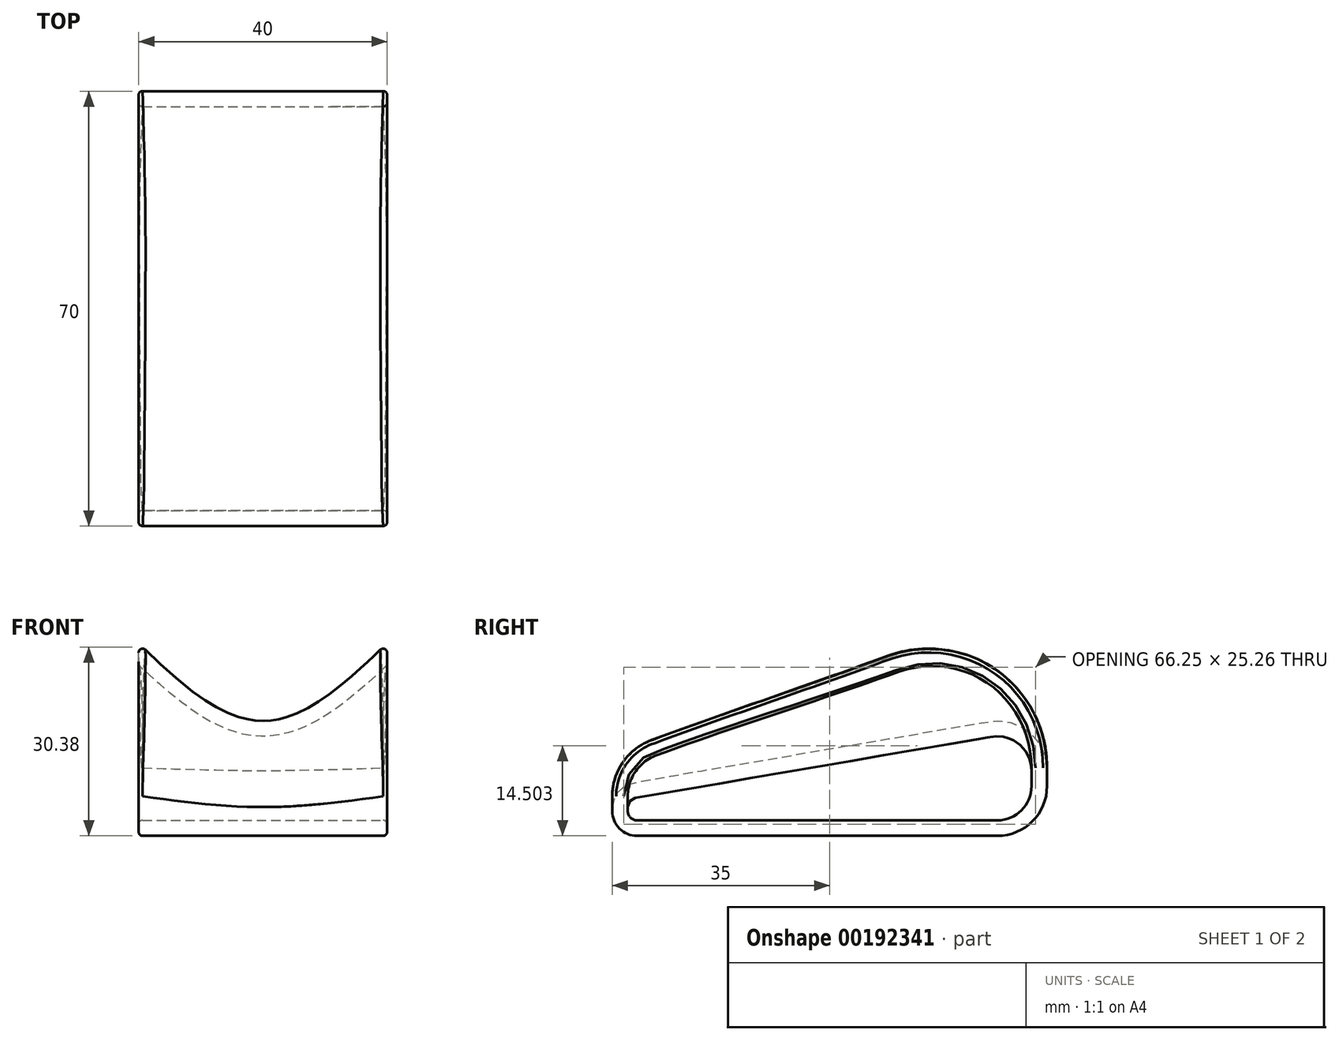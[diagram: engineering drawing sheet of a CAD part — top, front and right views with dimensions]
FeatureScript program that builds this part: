
annotation { "Feature Type Name" : "Feature", "Feature Type Description" : "" }
export const myFeature = defineFeature(function(context is Context, id is Id, definition is map)
    precondition{}
    {
        {
            assignVariable(context, id + "F0", {"name" : "Width", "anyValue" : 40});
        }
        {
            assignVariable(context, id + "F1", {"name" : "Thickness", "anyValue" : 2.5});
        }
        {
            var Q0;
            Q0=qCreatedBy(makeId("Right.planeOp"),FACE);
            var sketch = newSketch(context, id + "F2", { "sketchPlane" : qUnion([Q0])});
            skLineSegment(sketch, "E0", {"start": v(0, 0) * mm, "end": v(27, 0) * mm, "construction": true});
            skLineSegment(sketch, "E1", {"start": v(0, 0) * mm, "end": v(-31, 0) * mm, "construction": true});
            skLineSegment(sketch, "E2", {"start": v(-35, 4) * mm, "end": v(-35, 6.44) * mm, "construction": true});
            skLineSegment(sketch, "E3", {"start": v(35, 8) * mm, "end": v(35, 10.98) * mm, "construction": true});
            skLineSegment(sketch, "E4", {"start": v(7.88, 29.67) * mm, "end": v(-28.56, 15.79) * mm, "construction": true});
            skPoint(sketch, "E5.visualSharp", {"position": v(35, 40) * mm});
            skArc(sketch, "E5.filletArc", {"start": v(35, 10.98) * mm, "mid": v(26.35, 27.45) * mm, "end": v(7.88, 29.67) * mm, "construction": true});
            skPoint(sketch, "E6.visualSharp", {"position": v(-35, 13.33) * mm});
            skArc(sketch, "E6.filletArc", {"start": v(-28.56, 15.79) * mm, "mid": v(-33.23, 12.12) * mm, "end": v(-35, 6.44) * mm, "construction": true});
            skPoint(sketch, "E7.visualSharp", {"position": v(-35, 0) * mm});
            skArc(sketch, "E7.filletArc", {"start": v(-35, 4) * mm, "mid": v(-33.83, 1.17) * mm, "end": v(-31, 0) * mm, "construction": true});
            skPoint(sketch, "E8.visualSharp", {"position": v(35, 0) * mm});
            skArc(sketch, "E8.filletArc", {"start": v(27, 0) * mm, "mid": v(32.66, 2.34) * mm, "end": v(35, 8) * mm, "construction": true});
            skSolve(sketch);
        }
        {
            var Q0;
            Q0=qCreatedBy(makeId("Right.planeOp"),FACE);
            var sketch = newSketch(context, id + "F3", { "sketchPlane" : qUnion([Q0])});
            skLineSegment(sketch, "E9", {"start": v(0, 0) * mm, "end": v(27, 0) * mm, "construction": true});
            skLineSegment(sketch, "E10", {"start": v(0, 0) * mm, "end": v(-31, 0) * mm, "construction": true});
            skLineSegment(sketch, "E11", {"start": v(-35, 4) * mm, "end": v(-35, 4.63) * mm, "construction": true});
            skLineSegment(sketch, "E12", {"start": v(35, 8) * mm, "end": v(35, 10.51) * mm, "construction": true});
            skLineSegment(sketch, "E13", {"start": v(25.65, 18.4) * mm, "end": v(-31.68, 8.57) * mm, "construction": true});
            skPoint(sketch, "E14.visualSharp", {"position": v(35, 20) * mm});
            skArc(sketch, "E14.filletArc", {"start": v(35, 10.51) * mm, "mid": v(32.16, 16.63) * mm, "end": v(25.65, 18.4) * mm, "construction": true});
            skPoint(sketch, "E15.visualSharp", {"position": v(-35, 8) * mm});
            skArc(sketch, "E15.filletArc", {"start": v(-31.68, 8.57) * mm, "mid": v(-34.06, 7.2) * mm, "end": v(-35, 4.63) * mm, "construction": true});
            skPoint(sketch, "E16.visualSharp", {"position": v(-35, 0) * mm});
            skArc(sketch, "E16.filletArc", {"start": v(-35, 4) * mm, "mid": v(-33.83, 1.17) * mm, "end": v(-31, 0) * mm, "construction": true});
            skPoint(sketch, "E17.visualSharp", {"position": v(35, 0) * mm});
            skArc(sketch, "E17.filletArc", {"start": v(27, 0) * mm, "mid": v(32.66, 2.34) * mm, "end": v(35, 8) * mm, "construction": true});
            skSolve(sketch);
        }
        {
            var Q0;
            Q0=qCreatedBy(makeId("Right.planeOp"),FACE);
            cPlane(context, id + "F4", {"entities" : qUnion([Q0]), "cplaneType" : CPlaneType.OFFSET, "offset" : (getVariable(context, 'Width') * 2) * mm, "width" : 150 * mm, "height" : 150 * mm});
        }
        {
            var Q0;
            Q0=qCreatedBy(id+"F4.planeOp",FACE);
            cPlane(context, id + "F5", {"entities" : qUnion([Q0]), "cplaneType" : CPlaneType.OFFSET, "offset" : (getVariable(context, 'Width') / 2) * mm, "width" : 150 * mm, "height" : 150 * mm});
        }
        {
            var Q0;
            Q0=qCreatedBy(id+"F4.planeOp",FACE);
            cPlane(context, id + "F6", {"entities" : qUnion([Q0]), "cplaneType" : CPlaneType.OFFSET, "offset" : (getVariable(context, 'Width') / 2) * mm, "oppositeDirection" : true, "width" : 150 * mm, "height" : 150 * mm});
        }
        {
            var Q0;
            Q0=qCreatedBy(id+"F6.planeOp",FACE);
            var sketch = newSketch(context, id + "F7", { "sketchPlane" : qUnion([Q0])});
            skLineSegment(sketch, "E18.0", {"start": v(0, 0) * mm, "end": v(27, 0) * mm});
            skLineSegment(sketch, "E18.1", {"start": v(0, 0) * mm, "end": v(-31, 0) * mm});
            skLineSegment(sketch, "E18.2", {"start": v(-35, 4) * mm, "end": v(-35, 6.44) * mm});
            skLineSegment(sketch, "E18.3", {"start": v(35, 8) * mm, "end": v(35, 10.98) * mm});
            skLineSegment(sketch, "E18.4", {"start": v(7.88, 29.67) * mm, "end": v(-28.56, 15.79) * mm});
            skPoint(sketch, "E18.5", {"position": v(35, 40) * mm});
            skArc(sketch, "E18.6", {"start": v(35, 10.98) * mm, "mid": v(26.35, 27.45) * mm, "end": v(7.88, 29.67) * mm});
            skPoint(sketch, "E18.7", {"position": v(-35, 13.33) * mm});
            skArc(sketch, "E18.8", {"start": v(-28.56, 15.79) * mm, "mid": v(-33.23, 12.12) * mm, "end": v(-35, 6.44) * mm});
            skPoint(sketch, "E18.9", {"position": v(-35, 0) * mm});
            skArc(sketch, "E18.10", {"start": v(-35, 4) * mm, "mid": v(-33.83, 1.17) * mm, "end": v(-31, 0) * mm});
            skPoint(sketch, "E18.11", {"position": v(35, 0) * mm});
            skArc(sketch, "E18.12", {"start": v(27, 0) * mm, "mid": v(32.66, 2.34) * mm, "end": v(35, 8) * mm});
            skSolve(sketch);
        }
        {
            var Q0;
            Q0=qCreatedBy(id+"F4.planeOp",FACE);
            var sketch = newSketch(context, id + "F8", { "sketchPlane" : qUnion([Q0])});
            skLineSegment(sketch, "E19.0", {"start": v(0, 0) * mm, "end": v(27, 0) * mm});
            skLineSegment(sketch, "E19.1", {"start": v(0, 0) * mm, "end": v(-31, 0) * mm});
            skLineSegment(sketch, "E19.2", {"start": v(-35, 4) * mm, "end": v(-35, 4.63) * mm});
            skLineSegment(sketch, "E19.3", {"start": v(35, 8) * mm, "end": v(35, 10.51) * mm});
            skLineSegment(sketch, "E19.4", {"start": v(25.65, 18.4) * mm, "end": v(-31.68, 8.57) * mm});
            skPoint(sketch, "E19.5", {"position": v(35, 20) * mm});
            skArc(sketch, "E19.6", {"start": v(35, 10.51) * mm, "mid": v(32.16, 16.63) * mm, "end": v(25.65, 18.4) * mm});
            skPoint(sketch, "E19.7", {"position": v(-35, 8) * mm});
            skArc(sketch, "E19.8", {"start": v(-31.68, 8.57) * mm, "mid": v(-34.06, 7.2) * mm, "end": v(-35, 4.63) * mm});
            skPoint(sketch, "E19.9", {"position": v(-35, 0) * mm});
            skArc(sketch, "E19.10", {"start": v(-35, 4) * mm, "mid": v(-33.83, 1.17) * mm, "end": v(-31, 0) * mm});
            skPoint(sketch, "E19.11", {"position": v(35, 0) * mm});
            skArc(sketch, "E19.12", {"start": v(27, 0) * mm, "mid": v(32.66, 2.34) * mm, "end": v(35, 8) * mm});
            skSolve(sketch);
        }
        {
            var Q0;
            Q0=qCreatedBy(id+"F5.planeOp",FACE);
            var sketch = newSketch(context, id + "F9", { "sketchPlane" : qUnion([Q0])});
            skLineSegment(sketch, "E20.0", {"start": v(0, 0) * mm, "end": v(27, 0) * mm});
            skLineSegment(sketch, "E20.1", {"start": v(0, 0) * mm, "end": v(-31, 0) * mm});
            skLineSegment(sketch, "E20.2", {"start": v(-35, 4) * mm, "end": v(-35, 6.44) * mm});
            skLineSegment(sketch, "E20.3", {"start": v(35, 8) * mm, "end": v(35, 10.98) * mm});
            skLineSegment(sketch, "E20.4", {"start": v(7.88, 29.67) * mm, "end": v(-28.56, 15.79) * mm});
            skPoint(sketch, "E20.5", {"position": v(35, 40) * mm});
            skArc(sketch, "E20.6", {"start": v(35, 10.98) * mm, "mid": v(26.35, 27.45) * mm, "end": v(7.88, 29.67) * mm});
            skPoint(sketch, "E20.7", {"position": v(-35, 13.33) * mm});
            skArc(sketch, "E20.8", {"start": v(-28.56, 15.79) * mm, "mid": v(-33.23, 12.12) * mm, "end": v(-35, 6.44) * mm});
            skPoint(sketch, "E20.9", {"position": v(-35, 0) * mm});
            skArc(sketch, "E20.10", {"start": v(-35, 4) * mm, "mid": v(-33.83, 1.17) * mm, "end": v(-31, 0) * mm});
            skPoint(sketch, "E20.11", {"position": v(35, 0) * mm});
            skArc(sketch, "E20.12", {"start": v(27, 0) * mm, "mid": v(32.66, 2.34) * mm, "end": v(35, 8) * mm});
            skSolve(sketch);
        }
        {
            var Q0;
            Q0=makeQuery(id+"F7.imprint","IMPRINT",FACE,{"disambiguationData":[TD([[makeQuery(id+"F7.imprint","IMPRINT",EDGE,{"derivedFrom":sQuery(id+"F7.wireOp",EDGE,"E18.0")}),1.0]])]});
            var Q1;
            Q1=makeQuery(id+"F8.imprint","IMPRINT",FACE,{"disambiguationData":[TD([[makeQuery(id+"F8.imprint","IMPRINT",EDGE,{"derivedFrom":sQuery(id+"F8.wireOp",EDGE,"E19.0")}),1.0]])]});
            var Q2;
            Q2=makeQuery(id+"F9.imprint","IMPRINT",FACE,{"disambiguationData":[TD([[makeQuery(id+"F9.imprint","IMPRINT",EDGE,{"derivedFrom":sQuery(id+"F9.wireOp",EDGE,"E20.0")}),1.0]])]});
            var Q3;
            Q3=sQuery(id+"F7.wireOp",VERTEX,"E18.14.end");
            var Q4;
            Q4=sQuery(id+"F8.wireOp",VERTEX,"E19.14.end");
            var Q5;
            Q5=sQuery(id+"F9.wireOp",VERTEX,"E20.13.start");
            var Q6;
            Q6=sQuery(id+"F7.wireOp",VERTEX,"E18.19.start");
            var Q7;
            Q7=sQuery(id+"F8.wireOp",VERTEX,"E19.20.start");
            var Q8;
            Q8=sQuery(id+"F9.wireOp",VERTEX,"E20.19.start");
            loft(context, id + "F10", {"sheetProfilesArray" : [{ "sheetProfileEntities" : qUnion([Q0]) }, { "sheetProfileEntities" : qUnion([Q1]) }, { "sheetProfileEntities" : qUnion([Q2]) }], "connections" : [{ "connectionEntities" : qUnion([Q3, Q4, Q5, Q6, Q7, Q8]), "connectionEdgeQueries" : qUnion([]), "connectionEdgeParameters" : [] }]});
        }
        {
            var Q0;
            Q0=makeQuery(id+"F10.opLoft","CAP_FACE",FACE,{"disambiguationData":[OSD([makeQuery(id+"F9.imprint","IMPRINT",FACE,{"disambiguationData":[TD([[makeQuery(id+"F9.imprint","IMPRINT",EDGE,{"derivedFrom":sQuery(id+"F9.wireOp",EDGE,"E20.0")}),1.0]])]})])],"isStart":true});
            var Q1;
            Q1=makeQuery(id+"F10.opLoft","CAP_FACE",FACE,{"disambiguationData":[OSD([makeQuery(id+"F7.imprint","IMPRINT",FACE,{"disambiguationData":[TD([[makeQuery(id+"F7.imprint","IMPRINT",EDGE,{"derivedFrom":sQuery(id+"F7.wireOp",EDGE,"E18.0")}),1.0]])]})])],"isStart":true});
            shell(context, id + "F11", {"entities" : qUnion([Q0, Q1]), "thickness" : (getVariable(context, 'Thickness')) * mm});
        }
        {
            var Q0;
            Q0=makeQuery(id+"F10.opLoft","CAP_FACE",FACE,{"disambiguationData":[OSD([makeQuery(id+"F9.imprint","IMPRINT",FACE,{"disambiguationData":[TD([[makeQuery(id+"F9.imprint","IMPRINT",EDGE,{"derivedFrom":sQuery(id+"F9.wireOp",EDGE,"E20.0")}),1.0]])]})])],"isStart":true});
            var Q1;
            Q1=makeQuery(id+"F10.opLoft","CAP_FACE",FACE,{"disambiguationData":[OSD([makeQuery(id+"F7.imprint","IMPRINT",FACE,{"disambiguationData":[TD([[makeQuery(id+"F7.imprint","IMPRINT",EDGE,{"derivedFrom":sQuery(id+"F7.wireOp",EDGE,"E18.0")}),1.0]])]})])],"isStart":true});
            fillet(context, id + "F12", {"entities" : qUnion([Q0, Q1]), "radius" : (getVariable(context, 'Thickness') / 4) * mm, "tangentPropagation" : true, "allowEdgeOverflow" : false});
        }
    });
